# Revit family: 8.Пластинчатый рекуператор для прямоугольных каналов PR
name_source: partatom
category: Оборудование
revit_build: Autodesk Revit 2016 (Build: 20151209_0715(x64)
units: mm (PartAtom-declared; Revit-internal decimal feet)

## family parameters
Всегда вертикально = Да
На основе рабочей плоскости = Нет
Общий = Нет
При загрузке вырезать с полостями = Нет
Размер круглого соединителя = Использовать диаметр
Тип детали = Нормальный
Точка расчета площади = Нет

## types (9) — shared parameters
Единица измерения = шт.
Завод изготовитель = KORF
Ключевая пометка = Вентиляция
Материал = Сталь серая
Наименование и тех.хар-ка = Пластинчатый рекуператор для прямоугольных каналов
Раздел = ОВ
отступ = 15 мм

## per-type parameters (varying)
| type | А | Б | Высота | Г | Д | Е | Ж | Масса единицы | Н | Размер В | Тип, марка, обозначение | Ширина |
| 40-20 | 400 мм | 200 мм | 200 мм | 220 мм | 474 мм | 516 мм | 9 мм | 16,4 кг | 260 мм | 420 мм | PR 40-20 | 400 мм |
| 50-25 | 500 мм | 250 мм | 250 мм | 270 мм | 574 мм | 616 мм | 9 мм | 25,4 кг | 360 мм | 520 мм | PR 50-25 | 500 мм |
| 50-30 | 500 мм | 300 мм | 300 мм | 320 мм | 574 мм | 616 мм | 9 мм | 25,5 кг | 360 мм | 520 мм | PR 50-30 | 500 мм |
| 60-30 | 600 мм | 300 мм | 300 мм | 320 мм | 674 мм | 716 мм | 9 мм | 29,4 кг | 360 мм | 620 мм | PR 60-30 | 600 мм |
| 60-35 | 600 мм | 350 мм | 350 мм | 370 мм | 674 мм | 716 мм | 9 мм | 31,4 кг | 410 мм | 620 мм | PR 60-35 | 600 мм |
| 70-40 | 700 мм | 400 мм | 400 мм | 420 мм | 774 мм | 816 мм | 9 мм | 39,6 кг | 460 мм | 720 мм | PR 70-40 | 700 мм |
| 80-50 | 800 мм | 500 мм | 500 мм | 520 мм | 874 мм | 916 мм | 9 мм | 51,8 кг | 560 мм | 820 мм | PR 80-50 | 800 мм |
| 90-50 | 900 мм | 500 мм | 500 мм | 530 мм | 974 мм | 1016 мм | 11 мм | 64,4 кг | 560 мм | 930 мм | PR 90-50 | 900 мм |
| 100-50 | 1000 мм | 500 мм | 500 мм | 530 мм | 1074 мм | 1116 мм | 11 мм | 71,8 кг | 570 мм | 1030 мм | PR 100-50 | 1000 мм |
